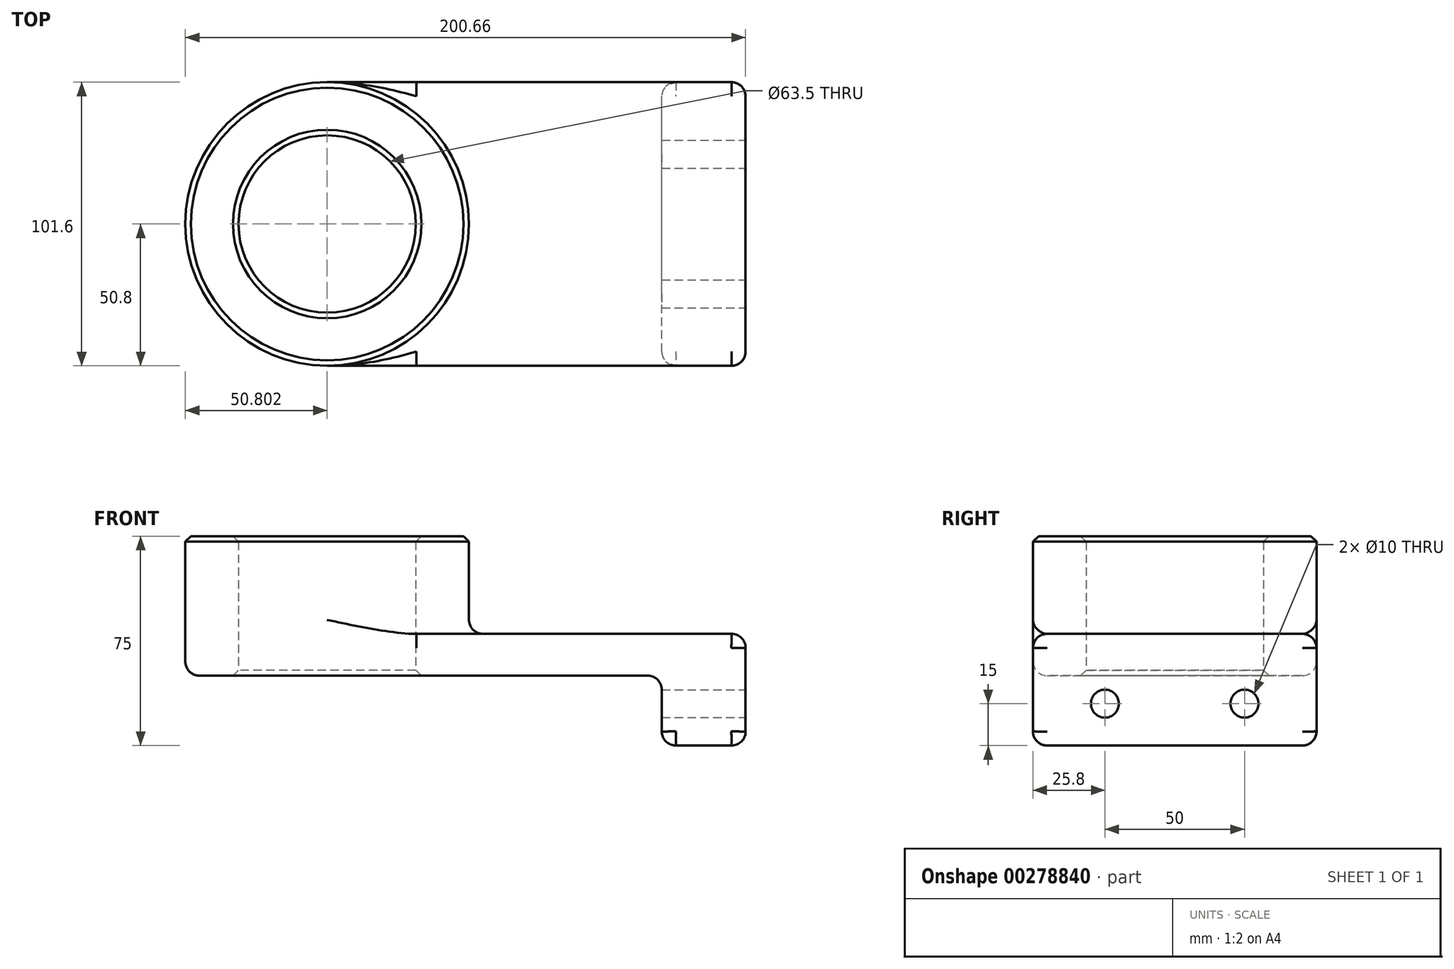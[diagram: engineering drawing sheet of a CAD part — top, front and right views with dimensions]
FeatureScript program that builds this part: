
annotation { "Feature Type Name" : "Feature", "Feature Type Description" : "" }
export const myFeature = defineFeature(function(context is Context, id is Id, definition is map)
    precondition{}
    {
        {
            var Q0;
            Q0=qCreatedBy(makeId("Top.planeOp"),FACE);
            var sketch = newSketch(context, id + "F0", { "sketchPlane" : qUnion([Q0])});
            skLineSegment(sketch, "E0.bottom", {"start": v(74.93, 50.8) * mm, "end": v(-74.93, 50.8) * mm});
            skLineSegment(sketch, "E0.top", {"start": v(74.93, -50.8) * mm, "end": v(-74.93, -50.8) * mm});
            skLineSegment(sketch, "E0.left", {"start": v(74.93, 50.8) * mm, "end": v(74.93, -50.8) * mm});
            skLineSegment(sketch, "E0.right", {"start": v(-74.93, 50.8) * mm, "end": v(-74.93, -50.8) * mm});
            skPoint(sketch, "E0.middle", {"position": v(0, 0) * mm});
            skCircle(sketch, "E1", {"center": v(-74.93, 0) * mm, "radius": 50.8 * mm});
            skCircle(sketch, "E2", {"center": v(-74.93, 0) * mm, "radius": 31.75 * mm});
            skSolve(sketch);
        }
        {
            var Q0;
            {var subQ0=sQuery(id+"F0.wireOp",EDGE,"E0.bottom");Q0=makeQuery(id+"F0.imprint","IMPRINT",FACE,{"disambiguationData":[TD([[makeQuery(id+"F0.imprint","IMPRINT",EDGE,{"derivedFrom":subQ0}),1.0]])]});}
            var Q1;
            {var subQ1=sQuery(id+"F0.wireOp",EDGE,"E0.right");var subQ3=sQuery(id+"F0.wireOp",EDGE,"E2");var subQ4=makeQuery(id+"F0.imprint","INTERSECT",VERTEX,{"disambiguationData":[OD(0.0)],"derivedFrom":[subQ1,subQ3]});Q1=makeQuery(id+"F0.imprint","IMPRINT",FACE,{"disambiguationData":[TD([[makeQuery(id+"F0.imprint","IMPRINT",EDGE,{"disambiguationData":[TD([[subQ4,1.0]])],"derivedFrom":subQ3}),-1.0]])]});}
            var Q2;
            {var subQ1=sQuery(id+"F0.wireOp",EDGE,"E0.right");var subQ3=sQuery(id+"F0.wireOp",EDGE,"E2");var subQ4=makeQuery(id+"F0.imprint","INTERSECT",VERTEX,{"disambiguationData":[OD(0.0)],"derivedFrom":[subQ1,subQ3]});Q2=makeQuery(id+"F0.imprint","IMPRINT",FACE,{"disambiguationData":[TD([[makeQuery(id+"F0.imprint","IMPRINT",EDGE,{"disambiguationData":[TD([[subQ4,-1.0]])],"derivedFrom":subQ3}),-1.0]])]});}
            var Q3;
            {var subQ0=sQuery(id+"F0.wireOp",EDGE,"E2");var subQ1=sQuery(id+"F0.wireOp",EDGE,"E0.right");var subQ2=makeQuery(id+"F0.imprint","INTERSECT",VERTEX,{"disambiguationData":[OD(0.0)],"derivedFrom":[subQ1,subQ0]});Q3=makeQuery(id+"F0.imprint","IMPRINT",FACE,{"disambiguationData":[TD([[makeQuery(id+"F0.imprint","IMPRINT",EDGE,{"disambiguationData":[TD([[subQ2,-1.0]])],"derivedFrom":subQ1}),-1.0]])]});}
            var Q4;
            {var subQ0=sQuery(id+"F0.wireOp",EDGE,"E2");var subQ1=sQuery(id+"F0.wireOp",EDGE,"E0.right");var subQ2=makeQuery(id+"F0.imprint","INTERSECT",VERTEX,{"disambiguationData":[OD(0.0)],"derivedFrom":[subQ1,subQ0]});Q4=makeQuery(id+"F0.imprint","IMPRINT",FACE,{"disambiguationData":[TD([[makeQuery(id+"F0.imprint","IMPRINT",EDGE,{"disambiguationData":[TD([[subQ2,-1.0]])],"derivedFrom":subQ1}),1.0]])]});}
            extrude(context, id + "F1", {"entities" : qUnion([Q0, Q1, Q2, Q3, Q4]), "depth" : 15 * mm});
        }
        {
            var Q0;
            {var subQ1=sQuery(id+"F0.wireOp",EDGE,"E0.right");var subQ3=sQuery(id+"F0.wireOp",EDGE,"E2");var subQ4=makeQuery(id+"F0.imprint","INTERSECT",VERTEX,{"disambiguationData":[OD(0.0)],"derivedFrom":[subQ1,subQ3]});Q0=makeQuery(id+"F0.imprint","IMPRINT",FACE,{"disambiguationData":[TD([[makeQuery(id+"F0.imprint","IMPRINT",EDGE,{"disambiguationData":[TD([[subQ4,-1.0]])],"derivedFrom":subQ3}),-1.0]])]});}
            var Q1;
            {var subQ1=sQuery(id+"F0.wireOp",EDGE,"E0.right");var subQ3=sQuery(id+"F0.wireOp",EDGE,"E2");var subQ4=makeQuery(id+"F0.imprint","INTERSECT",VERTEX,{"disambiguationData":[OD(0.0)],"derivedFrom":[subQ1,subQ3]});Q1=makeQuery(id+"F0.imprint","IMPRINT",FACE,{"disambiguationData":[TD([[makeQuery(id+"F0.imprint","IMPRINT",EDGE,{"disambiguationData":[TD([[subQ4,1.0]])],"derivedFrom":subQ3}),-1.0]])]});}
            extrude(context, id + "F2", {"entities" : qUnion([Q0, Q1]), "operationType" : NewBodyOperationType.ADD, "depth" : 50 * mm});
        }
        {
            var Q0;
            Q0=makeQuery(id+"F1.opExtrude","SWEPT_FACE",FACE,{"disambiguationData":[OSD([sQuery(id+"F0.wireOp",EDGE,"E0.left")])]});
            var sketch = newSketch(context, id + "F3", { "sketchPlane" : qUnion([Q0])});
            skLineSegment(sketch, "E3.bottom", {"start": v(-50.8, 15) * mm, "end": v(50.8, 15) * mm});
            skLineSegment(sketch, "E3.top", {"start": v(-50.8, -25) * mm, "end": v(50.8, -25) * mm});
            skLineSegment(sketch, "E3.left", {"start": v(-50.8, 15) * mm, "end": v(-50.8, -25) * mm});
            skLineSegment(sketch, "E3.right", {"start": v(50.8, 15) * mm, "end": v(50.8, -25) * mm});
            skCircle(sketch, "E4", {"center": v(-25, -10) * mm, "radius": 5 * mm});
            skLineSegment(sketch, "E5", {"start": v(0, 15) * mm, "end": v(0, -25) * mm, "construction": true});
            skCircle(sketch, "E6.MirrorC", {"center": v(25, -10) * mm, "radius": 5 * mm});
            skSolve(sketch);
        }
        {
            var Q0;
            {var subQ2=sQuery(id+"F3.wireOp",EDGE,"E3.top");Q0=makeQuery(id+"F3.imprint","IMPRINT",FACE,{"disambiguationData":[TD([[makeQuery(id+"F3.imprint","IMPRINT",EDGE,{"derivedFrom":subQ2}),1.0]])]});}
            var Q1;
            {var subQ0=sQuery(id+"F3.wireOp",EDGE,"E3.bottom");Q1=makeQuery(id+"F3.imprint","IMPRINT",FACE,{"disambiguationData":[TD([[makeQuery(id+"F3.imprint","IMPRINT",EDGE,{"derivedFrom":subQ0}),1.0]])]});}
            extrude(context, id + "F4", {"entities" : qUnion([Q0, Q1]), "operationType" : NewBodyOperationType.ADD, "oppositeDirection" : true, "depth" : 30 * mm});
        }
        {
            var Q0;
            Q0=makeQuery(id+"F1.opExtrude","CAP_EDGE",EDGE,{"disambiguationData":[OSD([sQuery(id+"F0.wireOp",EDGE,"E0.left")])],"isStart":false});
            var Q1;
            {var subQ0=sQuery(id+"F0.wireOp",EDGE,"E1");Q1=makeQuery(id+"F2.boolean.opBoolean","INTERSECT",EDGE,{"derivedFrom":[makeQuery(id+"F1.opExtrude","CAP_FACE",FACE,{"disambiguationData":[OSD([sQuery(id+"F0.wireOp",EDGE,"E0.bottom"),sQuery(id+"F0.wireOp",EDGE,"E0.top"),sQuery(id+"F0.wireOp",EDGE,"E0.left"),subQ0])],"isStart":false}),makeQuery(id+"F2.opExtrude","SWEPT_FACE",FACE,{"disambiguationData":[OSD([subQ0])]})]});}
            var Q2;
            Q2=makeQuery(id+"F4.opExtrude","CAP_EDGE",EDGE,{"disambiguationData":[OSD([sQuery(id+"F3.wireOp",EDGE,"E3.top")])],"isStart":true});
            var Q3;
            Q3=makeQuery(id+"F4.boolean.opBoolean","INTERSECT",EDGE,{"derivedFrom":[makeQuery(id+"F1.opExtrude","CAP_FACE",FACE,{"disambiguationData":[OSD([sQuery(id+"F0.wireOp",EDGE,"E0.bottom"),sQuery(id+"F0.wireOp",EDGE,"E0.top"),sQuery(id+"F0.wireOp",EDGE,"E0.left"),sQuery(id+"F0.wireOp",EDGE,"E1")])],"isStart":true}),makeQuery(id+"F4.opExtrude","CAP_FACE",FACE,{"disambiguationData":[OSD([sQuery(id+"F3.wireOp",EDGE,"E3.bottom"),sQuery(id+"F3.wireOp",EDGE,"E3.top"),sQuery(id+"F3.wireOp",EDGE,"E3.left"),sQuery(id+"F3.wireOp",EDGE,"E3.right"),sQuery(id+"F3.wireOp",EDGE,"E4"),sQuery(id+"F3.wireOp",EDGE,"E6.MirrorC")])],"isStart":false})]});
            var Q4;
            Q4=makeQuery(id+"F4.opExtrude","CAP_EDGE",EDGE,{"disambiguationData":[OSD([sQuery(id+"F3.wireOp",EDGE,"E3.top")])],"isStart":false});
            fillet(context, id + "F5", {"entities" : qUnion([Q0, Q1, Q2, Q3, Q4]), "radius" : 5 * mm, "tangentPropagation" : true, "allowEdgeOverflow" : false});
        }
        {
            var Q0;
            Q0=makeQuery(id+"F4.boolean.opBoolean","MERGE",FACE,{"derivedFrom":[makeQuery(id+"F1.opExtrude","SWEPT_FACE",FACE,{"disambiguationData":[OSD([sQuery(id+"F0.wireOp",EDGE,"E0.top")])]}),makeQuery(id+"F4.opExtrude","SWEPT_FACE",FACE,{"disambiguationData":[OSD([sQuery(id+"F3.wireOp",EDGE,"E3.left")])]})]});
            var Q1;
            Q1=makeQuery(id+"F4.boolean.opBoolean","MERGE",FACE,{"derivedFrom":[makeQuery(id+"F1.opExtrude","SWEPT_FACE",FACE,{"disambiguationData":[OSD([sQuery(id+"F0.wireOp",EDGE,"E0.bottom")])]}),makeQuery(id+"F4.opExtrude","SWEPT_FACE",FACE,{"disambiguationData":[OSD([sQuery(id+"F3.wireOp",EDGE,"E3.right")])]})]});
            fillet(context, id + "F6", {"entities" : qUnion([Q0, Q1]), "radius" : 5.08 * mm, "tangentPropagation" : true, "allowEdgeOverflow" : false});
        }
        {
            var Q0;
            Q0=makeQuery(id+"F2.opExtrude","CAP_EDGE",EDGE,{"disambiguationData":[OSD([sQuery(id+"F0.wireOp",EDGE,"E1")])],"isStart":false});
            var Q1;
            Q1=makeQuery(id+"F2.opExtrude","SWEPT_FACE",FACE,{"disambiguationData":[OSD([sQuery(id+"F0.wireOp",EDGE,"E2")])]});
            chamfer(context, id + "F7", {"entities" : qUnion([Q0, Q1]), "width" : 2 * mm, "tangentPropagation" : true});
        }
    });
